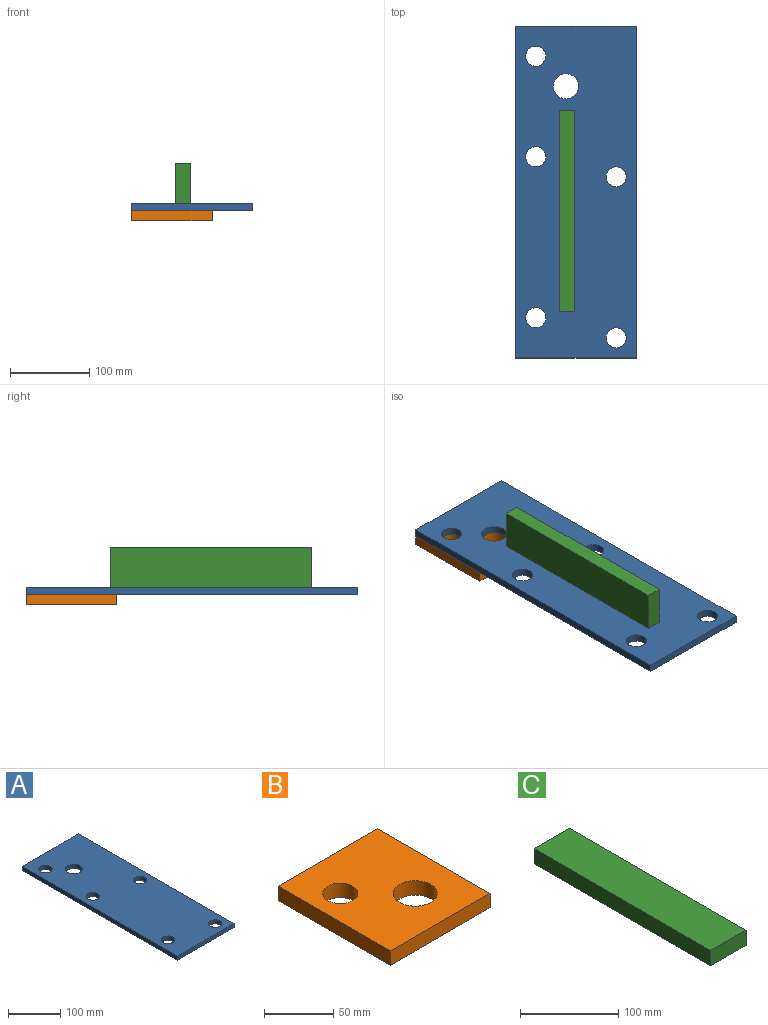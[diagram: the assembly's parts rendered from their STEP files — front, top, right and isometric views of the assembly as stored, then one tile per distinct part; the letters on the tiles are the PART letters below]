
ASSEMBLY  parts=3 mates=3
PART A: 12 faces, bbox 152.4x419.1x9.5 mm
  f0: plane 419.1x9.53mm, normal (-1,0,0), area 3991.9mm2, adj f1,f4,f10,f11
  f1: plane 152.4x9.53mm, normal (0,1,0), area 1451.6mm2, adj f0,f2,f10,f11
  f2: plane 419.1x9.53mm, normal (1,0,0), area 3991.9mm2, adj f1,f4,f10,f11
  f3: cylinder r=15.88mm len=31.75mm, axis (0,0,1), area 950.1mm2, adj f10,f11
  f4: plane 152.4x9.53mm, normal (0,-1,0), area 1451.6mm2, adj f0,f2,f10,f11
  f5: cylinder r=12.7mm len=25.4mm, axis (0,0,1), area 760.1mm2, adj f10,f11
  f6: cylinder r=12.7mm len=25.4mm, axis (0,0,1), area 760.1mm2, adj f10,f11
  f7: cylinder r=12.7mm len=25.4mm, axis (0,0,1), area 760.1mm2, adj f10,f11
  f8: cylinder r=12.7mm len=25.4mm, axis (0,0,1), area 760.1mm2, adj f10,f11
  f9: cylinder r=12.7mm len=25.4mm, axis (0,0,1), area 760.1mm2, adj f10,f11
  f10: plane 419.1x152.4mm, normal (0,0,-1), area 60545.6mm2, adj f0,f1,f2,f3,f4,f5,f6,f7
  f11: plane 419.1x152.4mm, normal (0,0,1), area 60545.6mm2, adj f0,f1,f2,f3,f4,f5,f6,f7
PART B: 8 faces, bbox 101.6x114.3x12.7 mm
  f0: plane 114.3x12.7mm, normal (-1,0,0), area 1451.6mm2, adj f1,f5,f6,f7
  f1: plane 101.6x12.7mm, normal (0,-1,0), area 1290.3mm2, adj f0,f2,f6,f7
  f2: plane 114.3x12.7mm, normal (1,0,0), area 1451.6mm2, adj f1,f5,f6,f7
  f3: cylinder r=15.88mm len=31.75mm, axis (0,0,-1), area 1266.8mm2, adj f6,f7
  f4: cylinder r=12.7mm len=25.4mm, axis (0,0,-1), area 1013.4mm2, adj f6,f7
  f5: plane 101.6x12.7mm, normal (0,1,0), area 1290.3mm2, adj f0,f2,f6,f7
  f6: plane 114.3x101.6mm, normal (0,0,1), area 10314.4mm2, adj f0,f1,f2,f3,f4,f5
  f7: plane 114.3x101.6mm, normal (0,0,-1), area 10314.4mm2, adj f0,f1,f2,f3,f4,f5
PART C: 6 faces, bbox 50.8x254x19.1 mm
  f0: plane 254x19.05mm, normal (-1,0,0), area 4838.7mm2, adj f1,f3,f4,f5
  f1: plane 50.8x19.05mm, normal (0,-1,0), area 967.7mm2, adj f0,f2,f4,f5
  f2: plane 254x19.05mm, normal (1,0,0), area 4838.7mm2, adj f1,f3,f4,f5
  f3: plane 50.8x19.05mm, normal (0,1,0), area 967.7mm2, adj f0,f2,f4,f5
  f4: plane 254x50.8mm, normal (0,0,1), area 12903.2mm2, adj f0,f1,f2,f3
  f5: plane 254x50.8mm, normal (0,0,-1), area 12903.2mm2, adj f0,f1,f2,f3
PLACE A t=(-38.1,38.1,22.22)mm
PLACE B t=(-38.1,38.1,0)mm
PLACE C rot(axis=(0.71,0,-0.71),180deg) t=(-27.49,-245.83,73.03)mm
MATE planar C.f2 <-> A.f11  axis (0,0,-1) through (-27.49,-118.83,22.22)mm
MATE cylindrical A.f3 <-> B.f3  axis (0,0,1) through (-38.1,38.1,12.7)mm
MATE planar A.f10 <-> B.f6  axis (0,0,-1) through (-24.81,-96.09,12.7)mm
